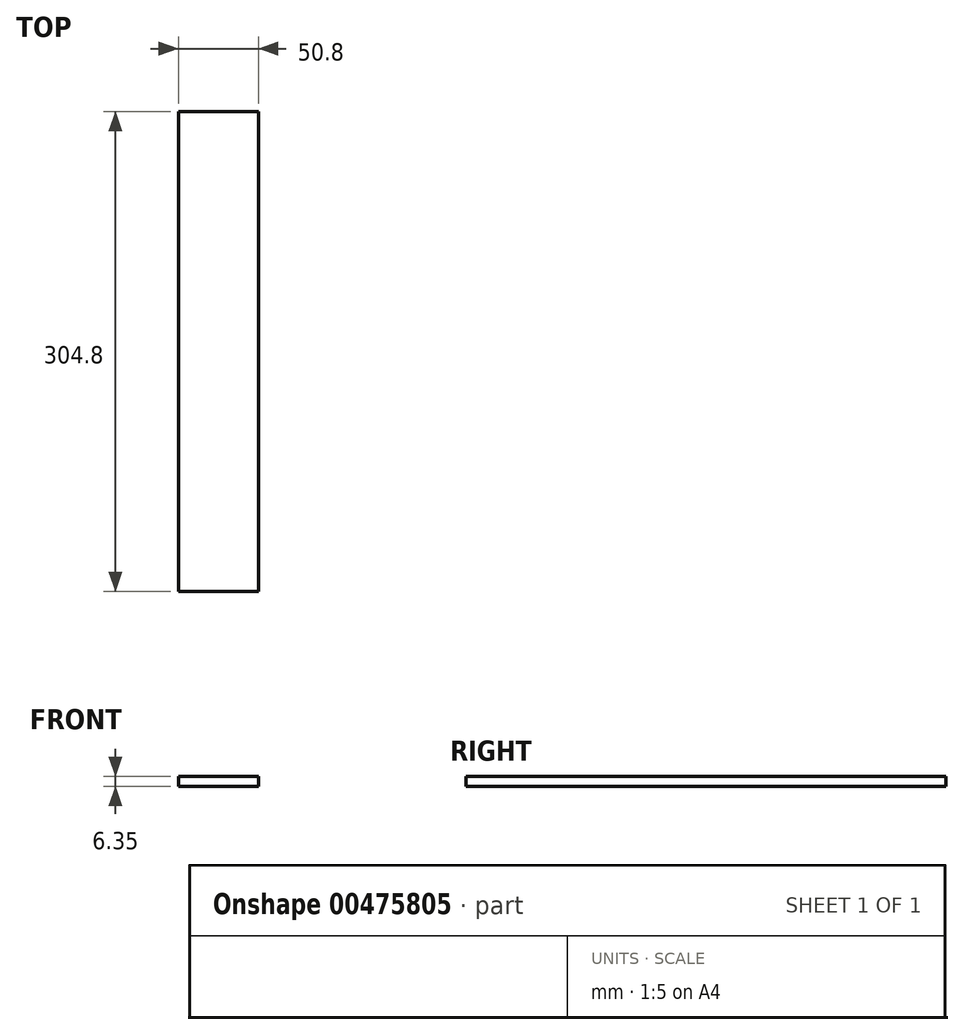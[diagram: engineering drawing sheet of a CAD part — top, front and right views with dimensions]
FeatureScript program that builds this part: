
annotation { "Feature Type Name" : "Feature", "Feature Type Description" : "" }
export const myFeature = defineFeature(function(context is Context, id is Id, definition is map)
    precondition{}
    {
        {
            var Q0;
            Q0=qCreatedBy(makeId("Front.planeOp"),FACE);
            var sketch = newSketch(context, id + "F0", { "sketchPlane" : qUnion([Q0])});
            skLineSegment(sketch, "E0.bottom", {"start": v(14.46, -4.78) * mm, "end": v(-36.34, -4.78) * mm});
            skLineSegment(sketch, "E0.top", {"start": v(14.46, -11.13) * mm, "end": v(-36.34, -11.13) * mm});
            skLineSegment(sketch, "E0.left", {"start": v(14.46, -4.78) * mm, "end": v(14.46, -11.13) * mm});
            skLineSegment(sketch, "E0.right", {"start": v(-36.34, -4.78) * mm, "end": v(-36.34, -11.13) * mm});
            skSolve(sketch);
        }
        {
            var Q0;
            Q0 = qSketchRegion(id + "F0", true);
            extrude(context, id + "F1", {"entities" : qUnion([Q0]), "depth" : 304.8 * mm});
        }
    });
